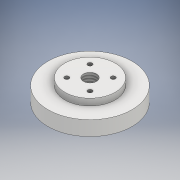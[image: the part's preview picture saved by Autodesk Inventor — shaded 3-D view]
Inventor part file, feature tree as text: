
AUTODESK INVENTOR PART (.ipt)
format: ipt  version: 2018 (Build 220112000, 112)  size: 128,000 bytes
history: native  units: mm
features: hole x2, sketch x2, revolve x1
ambient origin geometry x8: Origin, YZ Plane, XZ Plane, XY Plane, X Axis, Y Axis, Z Axis, Center Point
bodies: Solid1 (feature_tree)
feature tree (5):
  revolve  "Revolution1"  [1 undecoded]
  hole  "Hole1"  [1 undecoded]
  hole  "Hole2"  [1 undecoded]
  sketch  "Sketch1"  dims[d0=30.0mm d1=10.0mm]
  sketch  "Sketch3"  dims[d2=12.7mm d3=4.0mm d4=90.0deg d5=10.0mm d6=10.0mm d7=7.798mm d8=19.05mm d9=4.0mm d10=2.0mm d11=90.0deg d12=26.988mm d13=20.594885mm d14=19.558mm d15=2.642mm d16=7.01mm d17=7.145mm d18=3.505mm d19=90.0deg d20=10.979mm d21=20.594885mm]
note: 3 required parameter values undecoded (feature->parameter linkage not recoverable at this tier; creation-order binding heuristic only, values carry confidence <= 0.55)